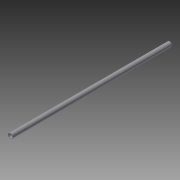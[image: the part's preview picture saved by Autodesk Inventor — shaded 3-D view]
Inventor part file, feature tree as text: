
AUTODESK INVENTOR PART (.ipt)
format: ipt  version: 2015 SP1 (Build 190203100, 203)  size: 69,120 bytes
history: native  units: mm
features: extrude x1, sketch x1
ambient origin geometry x8: Origin, YZ Plane, XZ Plane, XY Plane, X Axis, Y Axis, Z Axis, Center Point
bodies: Solid1 (feature_tree)
feature tree (2):
  extrude  "Extrusion1"  Depth=2300.0mm
  sketch  "Sketch1"  dims[d0=70.0mm d1=62.0mm d2=2300.0mm d3=0.0mm]
